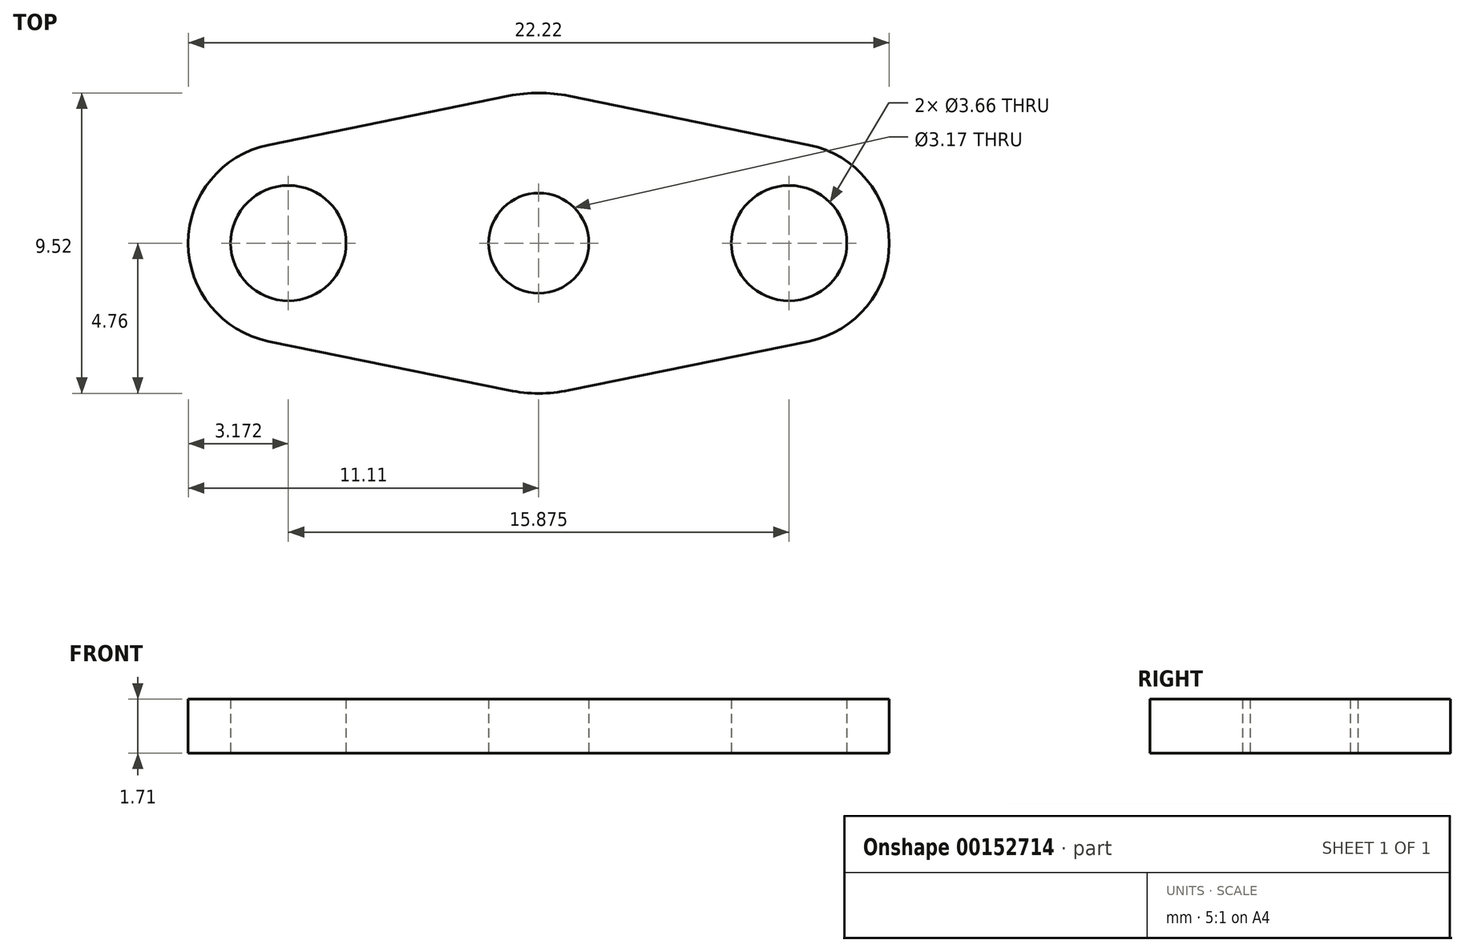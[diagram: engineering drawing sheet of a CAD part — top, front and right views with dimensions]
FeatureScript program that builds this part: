
annotation { "Feature Type Name" : "Feature", "Feature Type Description" : "" }
export const myFeature = defineFeature(function(context is Context, id is Id, definition is map)
    precondition{}
    {
        {
            var Q0;
            Q0=qCreatedBy(makeId("Top.planeOp"),FACE);
            var sketch = newSketch(context, id + "F0", { "sketchPlane" : qUnion([Q0])});
            skCircle(sketch, "E0", {"center": v(0, 0) * mm, "radius": 1.59 * mm});
            skLineSegment(sketch, "E1", {"start": v(-7.94, 0) * mm, "end": v(7.94, 0) * mm, "construction": true});
            skCircle(sketch, "E2", {"center": v(-7.94, 0) * mm, "radius": 1.83 * mm});
            skCircle(sketch, "E3", {"center": v(7.94, 0) * mm, "radius": 1.83 * mm});
            skArc(sketch, "E4", {"start": v(-8.57, 3.11) * mm, "mid": v(-11.11, 0) * mm, "end": v(-8.57, -3.11) * mm});
            skArc(sketch, "E5", {"start": v(8.57, -3.11) * mm, "mid": v(11.11, 0) * mm, "end": v(8.57, 3.11) * mm});
            skArc(sketch, "E6", {"start": v(0.95, 4.67) * mm, "mid": v(0, 4.76) * mm, "end": v(-0.95, 4.67) * mm});
            skLineSegment(sketch, "E7", {"start": v(-8.57, 3.11) * mm, "end": v(-0.95, 4.67) * mm});
            skLineSegment(sketch, "E8", {"start": v(0.95, 4.67) * mm, "end": v(8.57, 3.11) * mm});
            skLineSegment(sketch, "E9", {"start": v(8.57, -3.11) * mm, "end": v(0.95, -4.67) * mm});
            skLineSegment(sketch, "E10", {"start": v(-8.57, -3.11) * mm, "end": v(-0.95, -4.67) * mm});
            skArc(sketch, "E11", {"start": v(-0.95, -4.67) * mm, "mid": v(0, -4.76) * mm, "end": v(0.95, -4.67) * mm});
            skSolve(sketch);
        }
        {
            var Q0;
            Q0=qSketchRegion(id+"F0",true);
            extrude(context, id + "F1", {"entities" : qUnion([Q0]), "depth" : 1.7 * mm});
        }
    });
